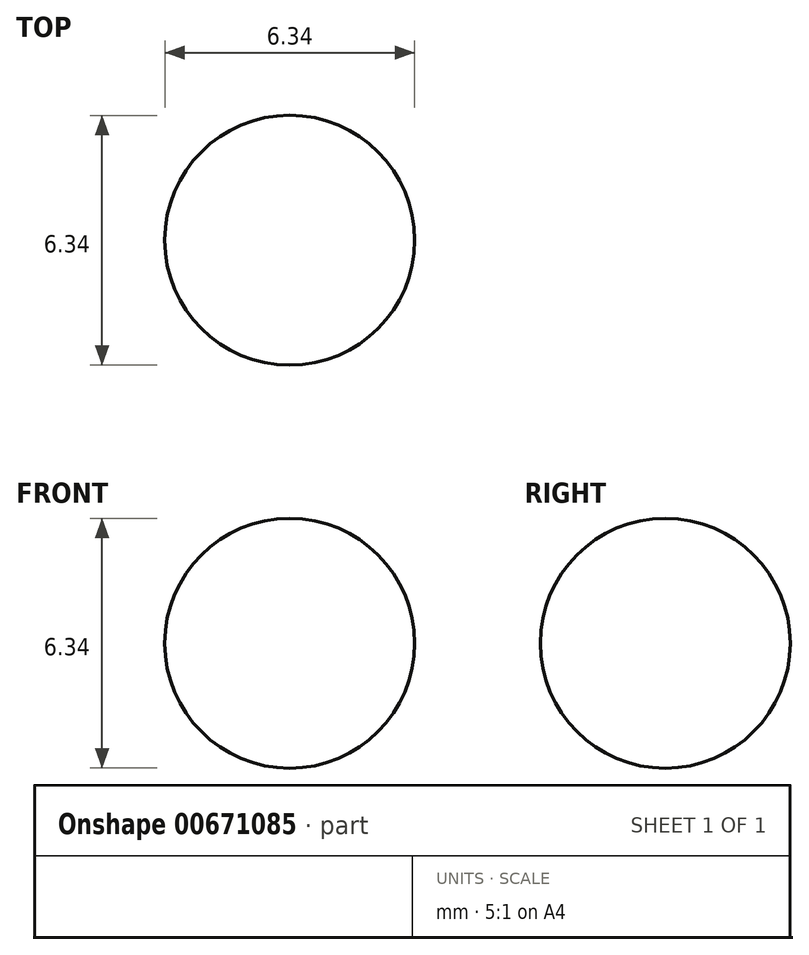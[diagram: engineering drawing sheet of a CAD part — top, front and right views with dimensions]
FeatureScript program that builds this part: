
annotation { "Feature Type Name" : "Feature", "Feature Type Description" : "" }
export const myFeature = defineFeature(function(context is Context, id is Id, definition is map)
    precondition{}
    {
        {
            var Q0;
            Q0=qCreatedBy(makeId("Front.planeOp"),FACE);
            var sketch = newSketch(context, id + "F0", { "sketchPlane" : qUnion([Q0])});
            skArc(sketch, "E0", {"start": v(3.18, 0) * mm, "mid": v(0, 3.18) * mm, "end": v(-3.18, 0) * mm});
            skLineSegment(sketch, "E1", {"start": v(-3.18, 0) * mm, "end": v(3.18, 0) * mm});
            skSolve(sketch);
        }
        {
            var Q0;
            Q0=qCreatedBy(makeId("Top.planeOp"),FACE);
            var sketch = newSketch(context, id + "F1", { "sketchPlane" : qUnion([Q0])});
            skLineSegment(sketch, "E2", {"start": v(63.48, 0) * mm, "end": v(-36.32, 0) * mm, "construction": true});
            skSolve(sketch);
        }
        {
            var Q0;
            Q0 = qSketchRegion(id + "F0", true);
            var Q1;
            Q1 = qConstructionFilter(qBodyType(qCreatedBy(id + "F0" ,EDGE), BodyType.WIRE), ConstructionObject.NO);
            var Q2;
            Q2=sQuery(id+"F1.wireOp",EDGE,"E2");
            revolve(context, id + "F2", {"entities" : qUnion([Q0]), "surfaceEntities" : qUnion([Q1]), "axis" : qUnion([Q2]), "revolveType" : RevolveType.FULL});
        }
    });
